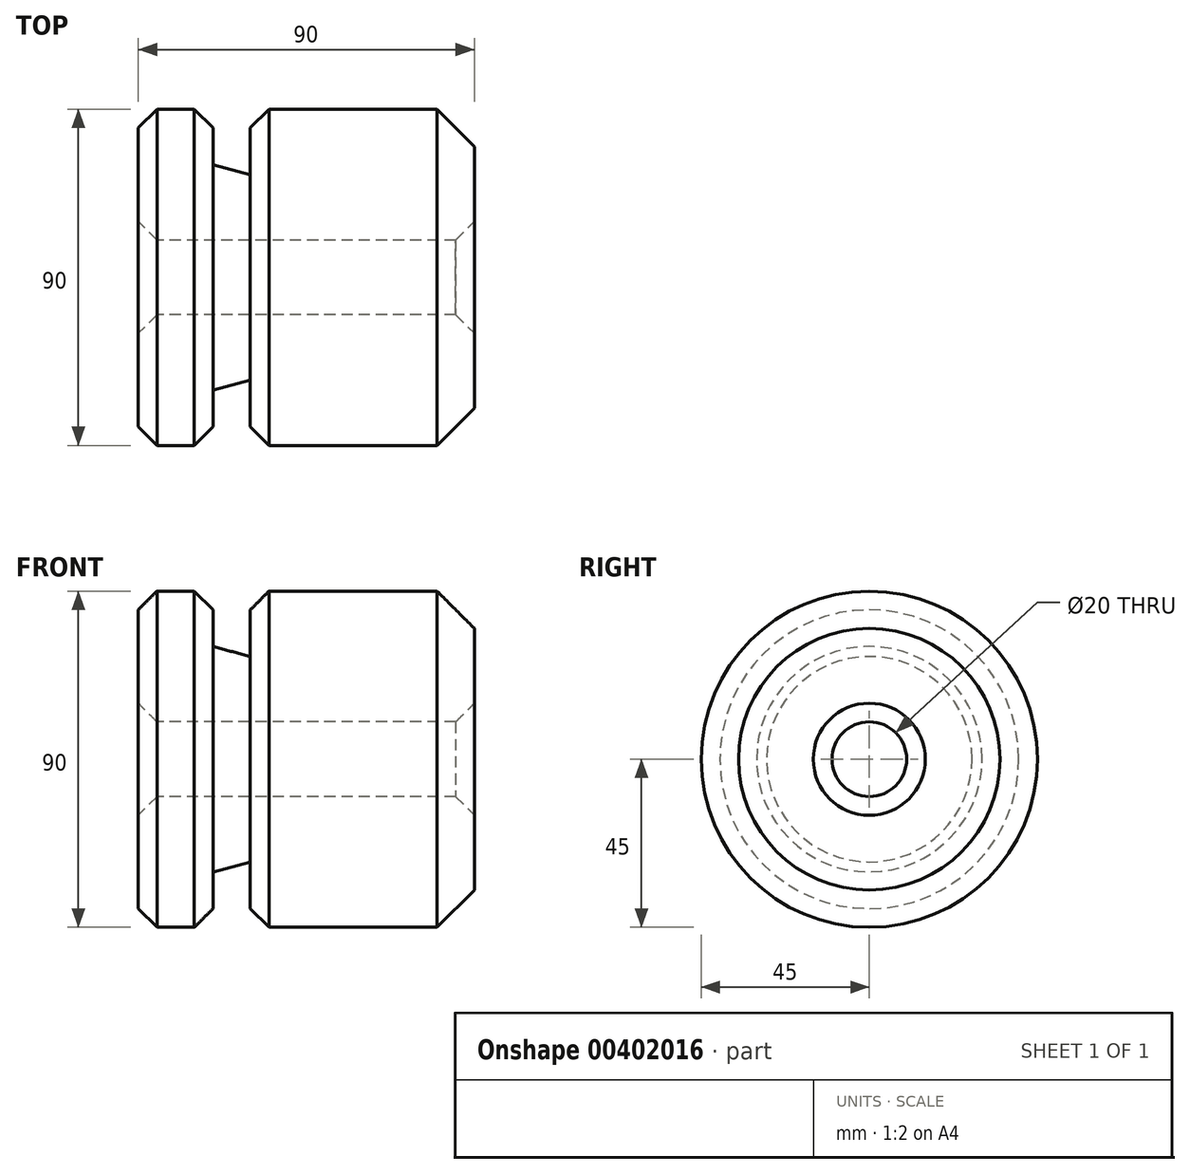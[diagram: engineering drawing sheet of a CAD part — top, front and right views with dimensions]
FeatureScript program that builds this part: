
annotation { "Feature Type Name" : "Feature", "Feature Type Description" : "" }
export const myFeature = defineFeature(function(context is Context, id is Id, definition is map)
    precondition{}
    {
        {
            var Q0;
            Q0=qCreatedBy(makeId("Front.planeOp"),FACE);
            var sketch = newSketch(context, id + "F0", { "sketchPlane" : qUnion([Q0])});
            skLineSegment(sketch, "E0", {"start": v(0, 0) * mm, "end": v(20, 0) * mm});
            skLineSegment(sketch, "E1", {"start": v(20, 0) * mm, "end": v(20, -14.82) * mm});
            skLineSegment(sketch, "E2", {"start": v(20, -14.82) * mm, "end": v(30, -17.5) * mm});
            skLineSegment(sketch, "E3", {"start": v(30, -17.5) * mm, "end": v(30, 0) * mm});
            skLineSegment(sketch, "E4", {"start": v(30, 0) * mm, "end": v(80, 0) * mm});
            skLineSegment(sketch, "E5", {"start": v(90, -35) * mm, "end": v(0, -35) * mm});
            skLineSegment(sketch, "E6", {"start": v(0, -35) * mm, "end": v(0, 0) * mm});
            skLineSegment(sketch, "E7", {"start": v(-26.3, -45) * mm, "end": v(115.2, -45) * mm, "construction": true});
            skLineSegment(sketch, "E8", {"start": v(90, -35) * mm, "end": v(90, -10) * mm});
            skLineSegment(sketch, "E9", {"start": v(90, -10) * mm, "end": v(80, 0) * mm});
            skSolve(sketch);
        }
        {
            var Q0;
            Q0 = qSketchRegion(id + "F0", true);
            var Q1;
            Q1=sQuery(id+"F0.wireOp",EDGE,"E7");
            revolve(context, id + "F1", {"entities" : qUnion([Q0]), "axis" : qUnion([Q1]), "revolveType" : RevolveType.FULL});
        }
        {
            var Q0;
            Q0=makeQuery(id+"F1.opRevolve","SWEPT_EDGE",EDGE,{"disambiguationData":[OSD([sQuery(id+"F0.wireOp",EDGE,"E0"),sQuery(id+"F0.wireOp",EDGE,"E6")])]});
            var Q1;
            Q1=makeQuery(id+"F1.opRevolve","SWEPT_EDGE",EDGE,{"disambiguationData":[OSD([sQuery(id+"F0.wireOp",EDGE,"E0"),sQuery(id+"F0.wireOp",EDGE,"E1")])]});
            var Q2;
            Q2=makeQuery(id+"F1.opRevolve","SWEPT_EDGE",EDGE,{"disambiguationData":[OSD([sQuery(id+"F0.wireOp",EDGE,"E3"),sQuery(id+"F0.wireOp",EDGE,"E4")])]});
            var Q3;
            Q3=makeQuery(id+"F1.opRevolve","SWEPT_EDGE",EDGE,{"disambiguationData":[OSD([sQuery(id+"F0.wireOp",EDGE,"E5"),sQuery(id+"F0.wireOp",EDGE,"E6")])]});
            var Q4;
            Q4=makeQuery(id+"F1.opRevolve","SWEPT_EDGE",EDGE,{"disambiguationData":[OSD([sQuery(id+"F0.wireOp",EDGE,"E5"),sQuery(id+"F0.wireOp",EDGE,"E8")])]});
            chamfer(context, id + "F2", {"entities" : qUnion([Q0, Q1, Q2, Q3, Q4]), "width" : 5 * mm, "tangentPropagation" : true});
        }
    });
